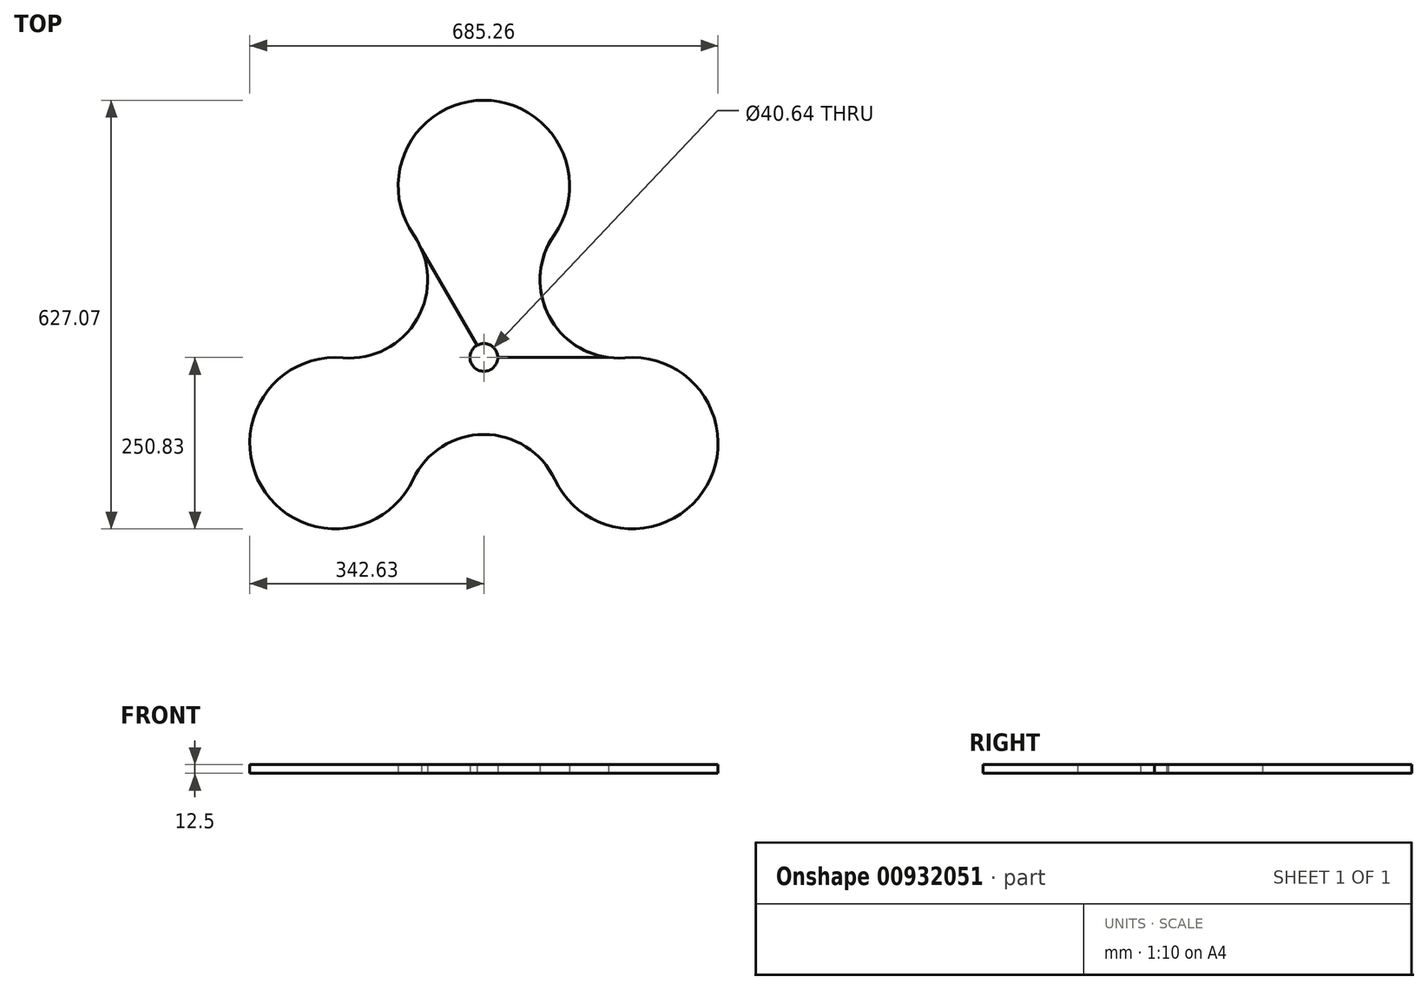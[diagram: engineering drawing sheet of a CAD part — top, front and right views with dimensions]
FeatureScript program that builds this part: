
annotation { "Feature Type Name" : "Feature", "Feature Type Description" : "" }
export const myFeature = defineFeature(function(context is Context, id is Id, definition is map)
    precondition{}
    {
        {
            var Q0;
            Q0=qCreatedBy(makeId("Top.planeOp"),FACE);
            var sketch = newSketch(context, id + "F0", { "sketchPlane" : qUnion([Q0])});
            skCircle(sketch, "E0", {"center": v(0, 0) * mm, "radius": 20.32 * mm});
            skCircle(sketch, "E1", {"center": v(0, 0) * mm, "radius": 65.09 * mm, "construction": true});
            skCircle(sketch, "E2", {"center": v(0, 0) * mm, "radius": 100.01 * mm});
            skLineSegment(sketch, "E3", {"start": v(0, 0) * mm, "end": v(0, 383.92) * mm, "construction": true});
            skCircle(sketch, "E4", {"center": v(0, 0) * mm, "radius": 250.83 * mm, "construction": true});
            skCircle(sketch, "E5", {"center": v(0, 0) * mm, "radius": 227.01 * mm, "construction": true});
            skLineSegment(sketch, "E6.1.0", {"start": v(0, 0) * mm, "end": v(-332.48, 191.96) * mm, "construction": true});
            skLineSegment(sketch, "E6.2.0", {"start": v(0, 0) * mm, "end": v(-332.48, -191.96) * mm, "construction": true});
            skLineSegment(sketch, "E6.3.0", {"start": v(0, 0) * mm, "end": v(0, -383.92) * mm, "construction": true});
            skLineSegment(sketch, "E6.4.0", {"start": v(0, 0) * mm, "end": v(332.48, -191.96) * mm, "construction": true});
            skLineSegment(sketch, "E6.5.0", {"start": v(0, 0) * mm, "end": v(332.48, 191.96) * mm, "construction": true});
            skArc(sketch, "E7", {"start": v(102.82, 179.01) * mm, "mid": v(0, 376.24) * mm, "end": v(-102.82, 179.01) * mm});
            skArc(sketch, "E8", {"start": v(102.82, 179.01) * mm, "mid": v(97.53, 56.3) * mm, "end": v(206.44, -0.46) * mm});
            skArc(sketch, "E9.1.0", {"start": v(-206.44, -0.46) * mm, "mid": v(-325.83, -188.12) * mm, "end": v(-103.62, -178.55) * mm});
            skArc(sketch, "E9.1.1", {"start": v(-206.44, -0.46) * mm, "mid": v(-97.53, 56.3) * mm, "end": v(-102.82, 179.01) * mm});
            skArc(sketch, "E9.2.0", {"start": v(103.62, -178.55) * mm, "mid": v(325.83, -188.12) * mm, "end": v(206.44, -0.46) * mm});
            skArc(sketch, "E9.2.1", {"start": v(103.62, -178.55) * mm, "mid": v(0, -112.62) * mm, "end": v(-103.62, -178.55) * mm});
            skSolve(sketch);
        }
        {
            var Q0;
            Q0=makeQuery(id+"F0.imprint","IMPRINT",FACE,{"disambiguationData":[TD([[makeQuery(id+"F0.imprint","IMPRINT",EDGE,{"derivedFrom":sQuery(id+"F0.wireOp",EDGE,"E2")}),-1.0]])]});
            var Q1;
            Q1=makeQuery(id+"F0.imprint","IMPRINT",FACE,{"disambiguationData":[TD([[makeQuery(id+"F0.imprint","IMPRINT",EDGE,{"derivedFrom":sQuery(id+"F0.wireOp",EDGE,"E0")}),-1.0]])]});
            extrude(context, id + "F1", {"entities" : qUnion([Q0, Q1]), "depth" : 12.5 * mm, "offsetDistance" : 25 * mm});
        }
        {
            var Q0;
            Q0=qCreatedBy(makeId("Top.planeOp"),FACE);
            var sketch = newSketch(context, id + "F2", { "sketchPlane" : qUnion([Q0])});
            skLineSegment(sketch, "E10", {"start": v(0, 0) * mm, "end": v(0, 416.53) * mm, "construction": true});
            skLineSegment(sketch, "E11.1.0", {"start": v(-10.16, 17.6) * mm, "end": v(-208.27, 360.73) * mm, "construction": true});
            skLineSegment(sketch, "E11.2.0", {"start": v(0, 0) * mm, "end": v(-360.73, 208.27) * mm, "construction": true});
            skLineSegment(sketch, "E11.3.0", {"start": v(0, 0) * mm, "end": v(-416.53, 0) * mm, "construction": true});
            skLineSegment(sketch, "E11.4.0", {"start": v(0, 0) * mm, "end": v(-360.73, -208.27) * mm, "construction": true});
            skLineSegment(sketch, "E11.5.0", {"start": v(0, 0) * mm, "end": v(-208.27, -360.73) * mm, "construction": true});
            skLineSegment(sketch, "E11.6.0", {"start": v(0, 0) * mm, "end": v(0, -416.53) * mm, "construction": true});
            skLineSegment(sketch, "E11.7.0", {"start": v(0, 0) * mm, "end": v(208.27, -360.73) * mm, "construction": true});
            skLineSegment(sketch, "E11.8.0", {"start": v(0, 0) * mm, "end": v(360.73, -208.27) * mm, "construction": true});
            skLineSegment(sketch, "E11.9.0", {"start": v(20.32, 0) * mm, "end": v(416.53, 0) * mm, "construction": true});
            skLineSegment(sketch, "E11.10.0", {"start": v(0, 0) * mm, "end": v(360.73, 208.27) * mm, "construction": true});
            skLineSegment(sketch, "E11.11.0", {"start": v(0, 0) * mm, "end": v(208.27, 360.73) * mm, "construction": true});
            skPoint(sketch, "E11.center", {"position": v(0, 0) * mm});
            skArc(sketch, "E12.0", {"start": v(102.82, 179.01) * mm, "mid": v(92.06, 67.05) * mm, "end": v(182.37, 0) * mm});
            skArc(sketch, "E13.0", {"start": v(-91.18, 157.94) * mm, "mid": v(-96.44, 168.78) * mm, "end": v(-102.82, 179.01) * mm});
            skLineSegment(sketch, "E14", {"start": v(-10.16, 17.6) * mm, "end": v(-91.18, 157.94) * mm});
            skLineSegment(sketch, "E15", {"start": v(20.32, 0) * mm, "end": v(182.37, 0) * mm});
            skArc(sketch, "E16.0", {"start": v(20.32, 0) * mm, "mid": v(10.16, 17.6) * mm, "end": v(-10.16, 17.6) * mm});
            skArc(sketch, "E17.0", {"start": v(102.82, 179.01) * mm, "mid": v(0, 376.24) * mm, "end": v(-102.82, 179.01) * mm});
            skArc(sketch, "E18.0.0", {"start": v(-102.82, 179.01) * mm, "mid": v(-96.44, 168.78) * mm, "end": v(-91.18, 157.94) * mm});
            skArc(sketch, "E18.0.4", {"start": v(182.37, 0) * mm, "mid": v(92.06, 67.05) * mm, "end": v(102.82, 179.01) * mm});
            skPoint(sketch, "E19.trimOffspring.end.orphan", {"position": v(103.62, -178.55) * mm});
            skPoint(sketch, "E20.trimOffspring.end.orphan", {"position": v(-103.62, -178.55) * mm});
            skPoint(sketch, "E21.orphan", {"position": v(-206.44, -0.46) * mm});
            skPoint(sketch, "E22.trimOffspring.end.orphan", {"position": v(206.44, -0.46) * mm});
            skSolve(sketch);
        }
        {
            var Q0;
            Q0=makeQuery(id+"F2.imprint","IMPRINT",FACE,{"disambiguationData":[TD([[makeQuery(id+"F2.imprint","IMPRINT",EDGE,{"derivedFrom":sQuery(id+"F2.wireOp",EDGE,"E14")}),-1.0]])]});
            extrude(context, id + "F3", {"entities" : qUnion([Q0]), "depth" : 12.5 * mm, "offsetDistance" : 25 * mm});
        }
    });
